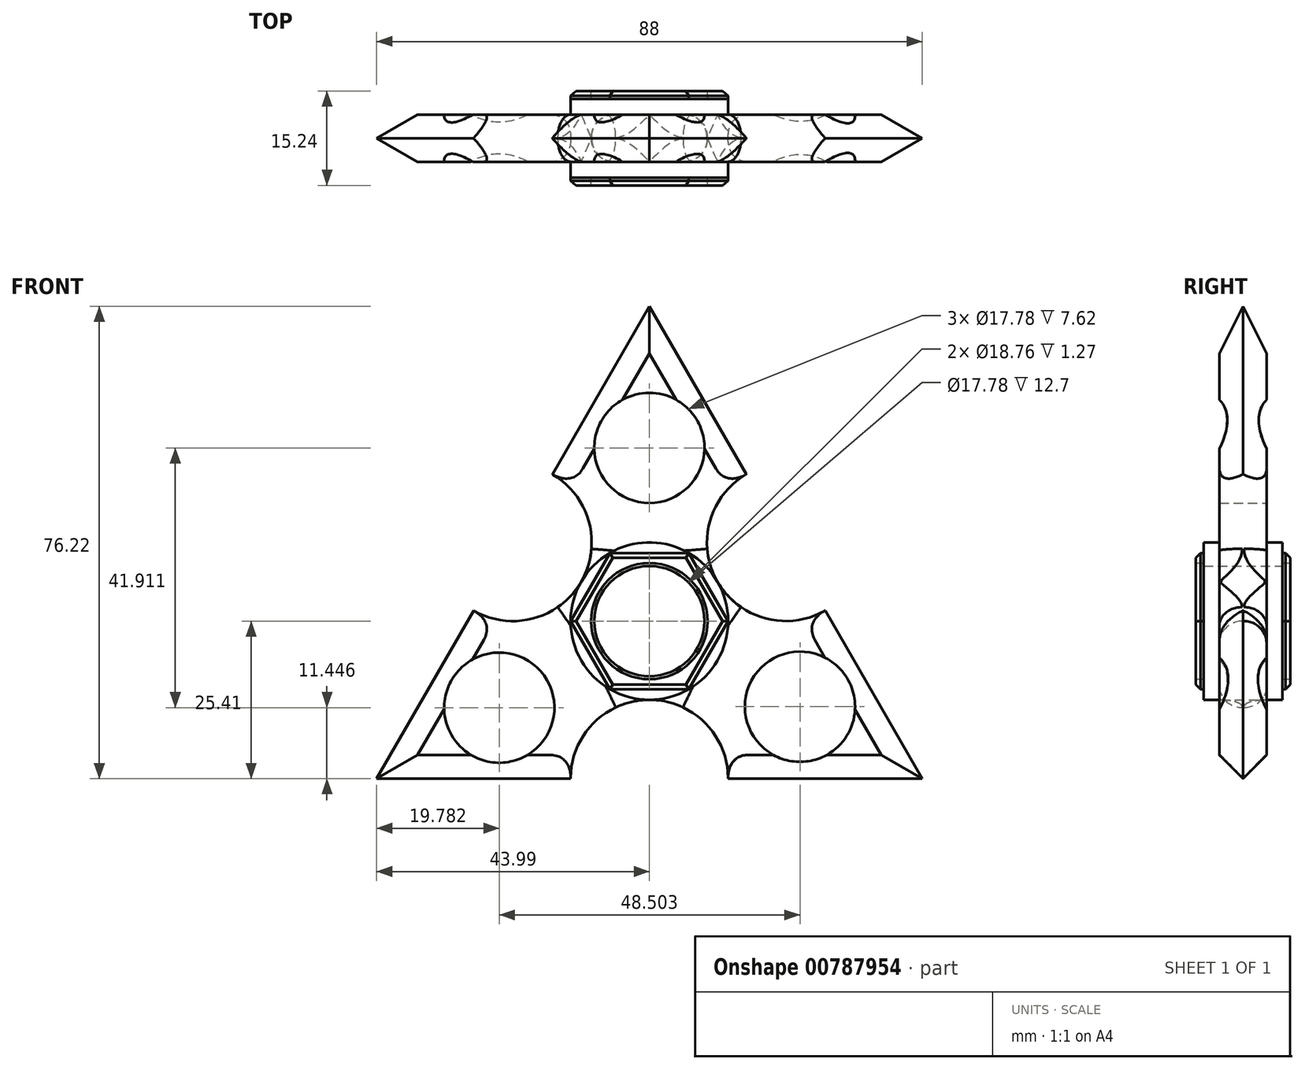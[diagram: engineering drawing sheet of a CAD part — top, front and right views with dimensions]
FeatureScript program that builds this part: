
annotation { "Feature Type Name" : "Feature", "Feature Type Description" : "" }
export const myFeature = defineFeature(function(context is Context, id is Id, definition is map)
    precondition{}
    {
        {
            var Q0;
            Q0=qCreatedBy(makeId("Front.planeOp"),FACE);
            var sketch = newSketch(context, id + "F0", { "sketchPlane" : qUnion([Q0])});
            skCircle(sketch, "E0.cCircle", {"center": v(0, 0) * mm, "radius": 25.4 * mm, "construction": true});
            skLineSegment(sketch, "E0.0", {"start": v(-0.01, 50.8) * mm, "end": v(44, -25.4) * mm});
            skLineSegment(sketch, "E0.1", {"start": v(44, -25.4) * mm, "end": v(-44, -25.41) * mm});
            skLineSegment(sketch, "E0.2", {"start": v(-44, -25.41) * mm, "end": v(-0.01, 50.8) * mm});
            skPoint(sketch, "E0.0.midPoint", {"position": v(22, 12.7) * mm});
            skCircle(sketch, "E1", {"center": v(-22, 12.7) * mm, "radius": 12.7 * mm});
            skCircle(sketch, "E2", {"center": v(0, -25.4) * mm, "radius": 12.7 * mm});
            skPoint(sketch, "E2.centerSnap0", {"position": v(0, -25.4) * mm});
            skCircle(sketch, "E3", {"center": v(22, 12.7) * mm, "radius": 12.7 * mm});
            skSolve(sketch);
        }
        {
            var Q0;
            {var subQ1=sQuery(id+"F0.wireOp",EDGE,"E0.0");var subQ8=sQuery(id+"F0.wireOp",EDGE,"E0.2");var subQ11=makeQuery(id+"F0.imprint","INTERSECT",VERTEX,{"derivedFrom":[subQ1,subQ8]});Q0=makeQuery(id+"F0.imprint","IMPRINT",FACE,{"disambiguationData":[TD([[makeQuery(id+"F0.imprint","IMPRINT",EDGE,{"disambiguationData":[TD([[subQ11,-1.0]])],"derivedFrom":subQ1}),-1.0]])]});}
            extrude(context, id + "F1", {"entities" : qUnion([Q0]), "depth" : 7.62 * mm, "offsetDistance" : 25.4 * mm});
        }
        {
            var Q0;
            Q0=makeQuery(id+"F1.opExtrude","CAP_FACE",FACE,{"disambiguationData":[OSD([sQuery(id+"F0.wireOp",EDGE,"E0.0"),sQuery(id+"F0.wireOp",EDGE,"E0.1"),sQuery(id+"F0.wireOp",EDGE,"E0.2"),sQuery(id+"F0.wireOp",EDGE,"E1"),sQuery(id+"F0.wireOp",EDGE,"E2"),sQuery(id+"F0.wireOp",EDGE,"E3")])],"isStart":false});
            var sketch = newSketch(context, id + "F2", { "sketchPlane" : qUnion([Q0])});
            skCircle(sketch, "E4", {"center": v(0, 0) * mm, "radius": 12.7 * mm});
            skSolve(sketch);
        }
        {
            var Q0;
            Q0=qSketchRegion(id+"F2",true);
            extrude(context, id + "F3", {"entities" : qUnion([Q0]), "operationType" : NewBodyOperationType.ADD, "depth" : 2.54 * mm, "offsetDistance" : 25.4 * mm, "hasSecondDirection" : true, "secondDirectionOppositeDirection" : true, "secondDirectionDepth" : 10.16 * mm});
        }
        {
            var Q0;
            Q0=makeQuery(id+"F3.opExtrude","CAP_FACE",FACE,{"disambiguationData":[OSD([sQuery(id+"F2.wireOp",EDGE,"E4")])],"isStart":true});
            var sketch = newSketch(context, id + "F4", { "sketchPlane" : qUnion([Q0])});
            skCircle(sketch, "E5", {"center": v(0, 0) * mm, "radius": 8.9 * mm});
            skSolve(sketch);
        }
        {
            var Q0;
            Q0=qSketchRegion(id+"F4",true);
            extrude(context, id + "F5", {"entities" : qUnion([Q0]), "operationType" : NewBodyOperationType.REMOVE, "oppositeDirection" : true, "depth" : 25.4 * mm, "offsetDistance" : 25.4 * mm});
        }
        {
            var Q0;
            Q0=makeQuery(id+"F1.opExtrude","CAP_FACE",FACE,{"disambiguationData":[OSD([sQuery(id+"F0.wireOp",EDGE,"E0.0"),sQuery(id+"F0.wireOp",EDGE,"E0.1"),sQuery(id+"F0.wireOp",EDGE,"E0.2"),sQuery(id+"F0.wireOp",EDGE,"E1"),sQuery(id+"F0.wireOp",EDGE,"E2"),sQuery(id+"F0.wireOp",EDGE,"E3")])],"isStart":true});
            var sketch = newSketch(context, id + "F6", { "sketchPlane" : qUnion([Q0])});
            skCircle(sketch, "E6", {"center": v(0, 27.95) * mm, "radius": 8.9 * mm});
            skCircle(sketch, "E7", {"center": v(-24.3, -13.82) * mm, "radius": 8.9 * mm});
            skCircle(sketch, "E8", {"center": v(24.2, -13.96) * mm, "radius": 8.9 * mm});
            skSolve(sketch);
        }
        {
            var Q0;
            Q0=qSketchRegion(id+"F6",true);
            extrude(context, id + "F7", {"entities" : qUnion([Q0]), "operationType" : NewBodyOperationType.REMOVE, "oppositeDirection" : true, "depth" : 25.4 * mm, "offsetDistance" : 25.4 * mm});
        }
        {
            var Q0;
            {var subQ0=sQuery(id+"F0.wireOp",EDGE,"E0.1");Q0=makeQuery(id+"F1.opExtrude","CAP_EDGE",EDGE,{"disambiguationData":[OSD([subQ0]),TDD([makeQuery(id+"F0.imprint","IMPRINT",EDGE,{"disambiguationData":[TD([[makeQuery(id+"F0.imprint","INTERSECT",VERTEX,{"derivedFrom":[subQ0,sQuery(id+"F0.wireOp",EDGE,"E0.2")]}),1.0]])],"derivedFrom":subQ0})])],"isStart":true});}
            var Q1;
            {var subQ0=sQuery(id+"F0.wireOp",EDGE,"E0.1");Q1=makeQuery(id+"F1.opExtrude","CAP_EDGE",EDGE,{"disambiguationData":[OSD([subQ0]),TDD([makeQuery(id+"F0.imprint","IMPRINT",EDGE,{"disambiguationData":[TD([[makeQuery(id+"F0.imprint","INTERSECT",VERTEX,{"derivedFrom":[subQ0,sQuery(id+"F0.wireOp",EDGE,"E0.2")]}),1.0]])],"derivedFrom":subQ0})])],"isStart":false});}
            var Q2;
            {var subQ0=sQuery(id+"F0.wireOp",EDGE,"E0.2");Q2=makeQuery(id+"F1.opExtrude","CAP_EDGE",EDGE,{"disambiguationData":[OSD([subQ0]),TDD([makeQuery(id+"F0.imprint","IMPRINT",EDGE,{"disambiguationData":[TD([[makeQuery(id+"F0.imprint","INTERSECT",VERTEX,{"derivedFrom":[sQuery(id+"F0.wireOp",EDGE,"E0.1"),subQ0]}),-1.0]])],"derivedFrom":subQ0})])],"isStart":true});}
            var Q3;
            {var subQ0=sQuery(id+"F0.wireOp",EDGE,"E0.2");Q3=makeQuery(id+"F1.opExtrude","CAP_EDGE",EDGE,{"disambiguationData":[OSD([subQ0]),TDD([makeQuery(id+"F0.imprint","IMPRINT",EDGE,{"disambiguationData":[TD([[makeQuery(id+"F0.imprint","INTERSECT",VERTEX,{"derivedFrom":[sQuery(id+"F0.wireOp",EDGE,"E0.1"),subQ0]}),-1.0]])],"derivedFrom":subQ0})])],"isStart":false});}
            var Q4;
            {var subQ0=sQuery(id+"F0.wireOp",EDGE,"E0.2");Q4=makeQuery(id+"F1.opExtrude","CAP_EDGE",EDGE,{"disambiguationData":[OSD([subQ0]),TDD([makeQuery(id+"F0.imprint","IMPRINT",EDGE,{"disambiguationData":[TD([[makeQuery(id+"F0.imprint","INTERSECT",VERTEX,{"derivedFrom":[sQuery(id+"F0.wireOp",EDGE,"E0.0"),subQ0]}),1.0]])],"derivedFrom":subQ0})])],"isStart":true});}
            var Q5;
            {var subQ0=sQuery(id+"F0.wireOp",EDGE,"E0.2");Q5=makeQuery(id+"F1.opExtrude","CAP_EDGE",EDGE,{"disambiguationData":[OSD([subQ0]),TDD([makeQuery(id+"F0.imprint","IMPRINT",EDGE,{"disambiguationData":[TD([[makeQuery(id+"F0.imprint","INTERSECT",VERTEX,{"derivedFrom":[sQuery(id+"F0.wireOp",EDGE,"E0.0"),subQ0]}),1.0]])],"derivedFrom":subQ0})])],"isStart":false});}
            var Q6;
            {var subQ0=sQuery(id+"F0.wireOp",EDGE,"E0.0");Q6=makeQuery(id+"F1.opExtrude","CAP_EDGE",EDGE,{"disambiguationData":[OSD([subQ0]),TDD([makeQuery(id+"F0.imprint","IMPRINT",EDGE,{"disambiguationData":[TD([[makeQuery(id+"F0.imprint","INTERSECT",VERTEX,{"derivedFrom":[subQ0,sQuery(id+"F0.wireOp",EDGE,"E0.2")]}),-1.0]])],"derivedFrom":subQ0})])],"isStart":true});}
            var Q7;
            {var subQ0=sQuery(id+"F0.wireOp",EDGE,"E0.0");Q7=makeQuery(id+"F1.opExtrude","CAP_EDGE",EDGE,{"disambiguationData":[OSD([subQ0]),TDD([makeQuery(id+"F0.imprint","IMPRINT",EDGE,{"disambiguationData":[TD([[makeQuery(id+"F0.imprint","INTERSECT",VERTEX,{"derivedFrom":[subQ0,sQuery(id+"F0.wireOp",EDGE,"E0.2")]}),-1.0]])],"derivedFrom":subQ0})])],"isStart":false});}
            var Q8;
            {var subQ0=sQuery(id+"F0.wireOp",EDGE,"E0.0");Q8=makeQuery(id+"F1.opExtrude","CAP_EDGE",EDGE,{"disambiguationData":[OSD([subQ0]),TDD([makeQuery(id+"F0.imprint","IMPRINT",EDGE,{"disambiguationData":[TD([[makeQuery(id+"F0.imprint","INTERSECT",VERTEX,{"derivedFrom":[subQ0,sQuery(id+"F0.wireOp",EDGE,"E0.1")]}),1.0]])],"derivedFrom":subQ0})])],"isStart":true});}
            var Q9;
            {var subQ0=sQuery(id+"F0.wireOp",EDGE,"E0.0");Q9=makeQuery(id+"F1.opExtrude","CAP_EDGE",EDGE,{"disambiguationData":[OSD([subQ0]),TDD([makeQuery(id+"F0.imprint","IMPRINT",EDGE,{"disambiguationData":[TD([[makeQuery(id+"F0.imprint","INTERSECT",VERTEX,{"derivedFrom":[subQ0,sQuery(id+"F0.wireOp",EDGE,"E0.1")]}),1.0]])],"derivedFrom":subQ0})])],"isStart":false});}
            var Q10;
            {var subQ0=sQuery(id+"F0.wireOp",EDGE,"E0.1");Q10=makeQuery(id+"F1.opExtrude","CAP_EDGE",EDGE,{"disambiguationData":[OSD([subQ0]),TDD([makeQuery(id+"F0.imprint","IMPRINT",EDGE,{"disambiguationData":[TD([[makeQuery(id+"F0.imprint","INTERSECT",VERTEX,{"derivedFrom":[sQuery(id+"F0.wireOp",EDGE,"E0.0"),subQ0]}),-1.0]])],"derivedFrom":subQ0})])],"isStart":true});}
            var Q11;
            {var subQ0=sQuery(id+"F0.wireOp",EDGE,"E0.1");Q11=makeQuery(id+"F1.opExtrude","CAP_EDGE",EDGE,{"disambiguationData":[OSD([subQ0]),TDD([makeQuery(id+"F0.imprint","IMPRINT",EDGE,{"disambiguationData":[TD([[makeQuery(id+"F0.imprint","INTERSECT",VERTEX,{"derivedFrom":[sQuery(id+"F0.wireOp",EDGE,"E0.0"),subQ0]}),-1.0]])],"derivedFrom":subQ0})])],"isStart":false});}
            chamfer(context, id + "F8", {"entities" : qUnion([Q0, Q1, Q2, Q3, Q4, Q5, Q6, Q7, Q8, Q9, Q10, Q11]), "width" : 3.8 * mm, "tangentPropagation" : true});
        }
        {
            var Q0;
            Q0=makeQuery(id+"F1.opExtrude","CAP_EDGE",EDGE,{"disambiguationData":[OSD([sQuery(id+"F0.wireOp",EDGE,"E2")])],"isStart":true});
            var Q1;
            Q1=makeQuery(id+"F1.opExtrude","CAP_EDGE",EDGE,{"disambiguationData":[OSD([sQuery(id+"F0.wireOp",EDGE,"E2")])],"isStart":false});
            var Q2;
            Q2=makeQuery(id+"F1.opExtrude","CAP_EDGE",EDGE,{"disambiguationData":[OSD([sQuery(id+"F0.wireOp",EDGE,"E1")])],"isStart":true});
            var Q3;
            Q3=makeQuery(id+"F1.opExtrude","CAP_EDGE",EDGE,{"disambiguationData":[OSD([sQuery(id+"F0.wireOp",EDGE,"E1")])],"isStart":false});
            var Q4;
            Q4=makeQuery(id+"F1.opExtrude","CAP_EDGE",EDGE,{"disambiguationData":[OSD([sQuery(id+"F0.wireOp",EDGE,"E3")])],"isStart":true});
            var Q5;
            Q5=makeQuery(id+"F1.opExtrude","CAP_EDGE",EDGE,{"disambiguationData":[OSD([sQuery(id+"F0.wireOp",EDGE,"E3")])],"isStart":false});
            fillet(context, id + "F9", {"entities" : qUnion([Q0, Q1, Q2, Q3, Q4, Q5]), "radius" : 3.68 * mm, "tangentPropagation" : true, "allowEdgeOverflow" : false});
        }
        {
            var Q0;
            Q0=makeQuery(id+"F3.opExtrude","CAP_FACE",FACE,{"disambiguationData":[OSD([sQuery(id+"F2.wireOp",EDGE,"E4")])],"isStart":false});
            var sketch = newSketch(context, id + "F10", { "sketchPlane" : qUnion([Q0])});
            skCircle(sketch, "E9.cCircle", {"center": v(0, 0) * mm, "radius": 12.7 * mm, "construction": true});
            skLineSegment(sketch, "E9.0", {"start": v(12.7, 0) * mm, "end": v(6.35, -11) * mm});
            skLineSegment(sketch, "E9.1", {"start": v(6.35, -11) * mm, "end": v(-6.35, -11) * mm});
            skLineSegment(sketch, "E9.2", {"start": v(-6.35, -11) * mm, "end": v(-12.7, 0) * mm});
            skLineSegment(sketch, "E9.3", {"start": v(-12.7, 0) * mm, "end": v(-6.35, 11) * mm});
            skLineSegment(sketch, "E9.4", {"start": v(-6.35, 11) * mm, "end": v(6.35, 11) * mm});
            skLineSegment(sketch, "E9.5", {"start": v(6.35, 11) * mm, "end": v(12.7, 0) * mm});
            skCircle(sketch, "E10", {"center": v(0, 0) * mm, "radius": 9.38 * mm});
            skSolve(sketch);
        }
        {
            var Q0;
            Q0=qSketchRegion(id+"F10",true);
            extrude(context, id + "F11", {"entities" : qUnion([Q0]), "operationType" : NewBodyOperationType.ADD, "depth" : 1.27 * mm, "offsetDistance" : 25.4 * mm, "hasSecondDirection" : true, "secondDirectionOppositeDirection" : true, "secondDirectionDepth" : 13.97 * mm});
        }
        {
            var Q0;
            Q0=makeQuery(id+"F11.opExtrude","CAP_EDGE",EDGE,{"disambiguationData":[OSD([sQuery(id+"F10.wireOp",EDGE,"E9.4")])],"isStart":true});
            var Q1;
            Q1=makeQuery(id+"F11.opExtrude","CAP_EDGE",EDGE,{"disambiguationData":[OSD([sQuery(id+"F10.wireOp",EDGE,"E9.5")])],"isStart":true});
            var Q2;
            Q2=makeQuery(id+"F11.opExtrude","CAP_EDGE",EDGE,{"disambiguationData":[OSD([sQuery(id+"F10.wireOp",EDGE,"E9.0")])],"isStart":true});
            var Q3;
            Q3=makeQuery(id+"F11.opExtrude","CAP_EDGE",EDGE,{"disambiguationData":[OSD([sQuery(id+"F10.wireOp",EDGE,"E9.1")])],"isStart":true});
            var Q4;
            Q4=makeQuery(id+"F11.opExtrude","CAP_EDGE",EDGE,{"disambiguationData":[OSD([sQuery(id+"F10.wireOp",EDGE,"E9.2")])],"isStart":true});
            var Q5;
            Q5=makeQuery(id+"F11.opExtrude","CAP_EDGE",EDGE,{"disambiguationData":[OSD([sQuery(id+"F10.wireOp",EDGE,"E9.3")])],"isStart":true});
            var Q6;
            Q6=makeQuery(id+"F11.opExtrude","CAP_EDGE",EDGE,{"disambiguationData":[OSD([sQuery(id+"F10.wireOp",EDGE,"E9.5")])],"isStart":false});
            var Q7;
            Q7=makeQuery(id+"F11.opExtrude","CAP_EDGE",EDGE,{"disambiguationData":[OSD([sQuery(id+"F10.wireOp",EDGE,"E9.0")])],"isStart":false});
            var Q8;
            Q8=makeQuery(id+"F11.opExtrude","CAP_EDGE",EDGE,{"disambiguationData":[OSD([sQuery(id+"F10.wireOp",EDGE,"E9.4")])],"isStart":false});
            var Q9;
            Q9=makeQuery(id+"F11.opExtrude","CAP_EDGE",EDGE,{"disambiguationData":[OSD([sQuery(id+"F10.wireOp",EDGE,"E9.3")])],"isStart":false});
            var Q10;
            Q10=makeQuery(id+"F11.opExtrude","CAP_EDGE",EDGE,{"disambiguationData":[OSD([sQuery(id+"F10.wireOp",EDGE,"E9.2")])],"isStart":false});
            var Q11;
            Q11=makeQuery(id+"F11.opExtrude","CAP_EDGE",EDGE,{"disambiguationData":[OSD([sQuery(id+"F10.wireOp",EDGE,"E9.1")])],"isStart":false});
            chamfer(context, id + "F12", {"entities" : qUnion([Q0, Q1, Q2, Q3, Q4, Q5, Q6, Q7, Q8, Q9, Q10, Q11]), "width" : 0.76 * mm, "tangentPropagation" : true});
        }
    });
